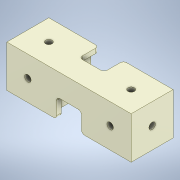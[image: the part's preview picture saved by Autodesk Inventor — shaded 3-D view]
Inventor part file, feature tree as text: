
AUTODESK INVENTOR PART (.ipt)
format: ipt  version: 2022.1 (Build 261234020, 234B)  size: 290,816 bytes
history: native  units: in
note: dims shown in document units (in); Inventor stores cm internally (conversion verified against a paired STEP export)
features: sketch x10, extrude x7, hole x3, mirror x1, fillet x1, projected_geometry x1
ambient origin geometry x8: Origin, YZ Plane, XZ Plane, XY Plane, X Axis, Y Axis, Z Axis, Center Point
bodies: Solid1 (feature_tree)
feature tree (23):
  extrude  "Extrusion1"  Depth=1.063in
  sketch  "Sketch2"  dims[d2=1.063in d3=0.0in d4=0.5315in]
  sketch  "Sketch3"  dims[d5=0.5315in d6=0.5315in]
  hole  "Hole1"  [1 undecoded]
  hole  "Hole2"  [1 undecoded]
  hole  "Hole3"  [1 undecoded]
  extrude  "Extrusion2"  Depth=0.2185in
  extrude  "Extrusion3"  Depth=0.2185in
  extrude  "Extrusion4"  Depth=0.0787in
  extrude  "Extrusion16"  Depth=0.0787in TaperAngle=0.0deg
  mirror  "Mirror1"
  extrude  "Extrusion17"  Depth=0.1181in
  extrude  "Extrusion18"  Depth=0.0787in TaperAngle=0.0deg
  fillet  "Fillet1"  Radius=0.6299in
  sketch  "Sketch1"  dims[d0=1.063in d1=1.063in]
  sketch  "Sketch4"  dims[d7=0.5315in d8=0.5315in]
  sketch  "Sketch5"  dims[d9=0.5315in]
  sketch  "Sketch6"  dims[d10=0.126in d11=0.2362in d12=0.1654in d13=0.2165in d14=90.0deg d15=0.5906in d16=0.8108in]
  sketch  "Sketch7"  dims[d17=0.126in d18=0.2362in d19=0.1654in d20=0.2165in d21=90.0deg d22=0.5906in d23=0.8108in]
  sketch  "Sketch23"  dims[d24=0.126in d25=0.2362in d26=0.1654in d27=0.2165in d28=90.0deg d29=0.5906in d30=0.8108in d31=0.2185in]
  projected_geometry  "Projected Loop6"
  sketch  "Sketch24"  dims[d32=0.1772in d33=0.0in d34=0.2185in]
  sketch  "Sketch25"  dims[d35=0.1772in d36=0.0in d37=0.2185in d38=0.1772in d39=0.0in d77=0.1181in d78=0.5118in d79=0.0in d82=0.6299in d83=0.4921in d84=0.7874in d85=0.0in d86=0.6299in d87=0.4921in d88=0.7874in d89=0.0in d90=0.0787in]
note: 3 required parameter values undecoded (feature->parameter linkage not recoverable at this tier; creation-order binding heuristic only, values carry confidence <= 0.55)
